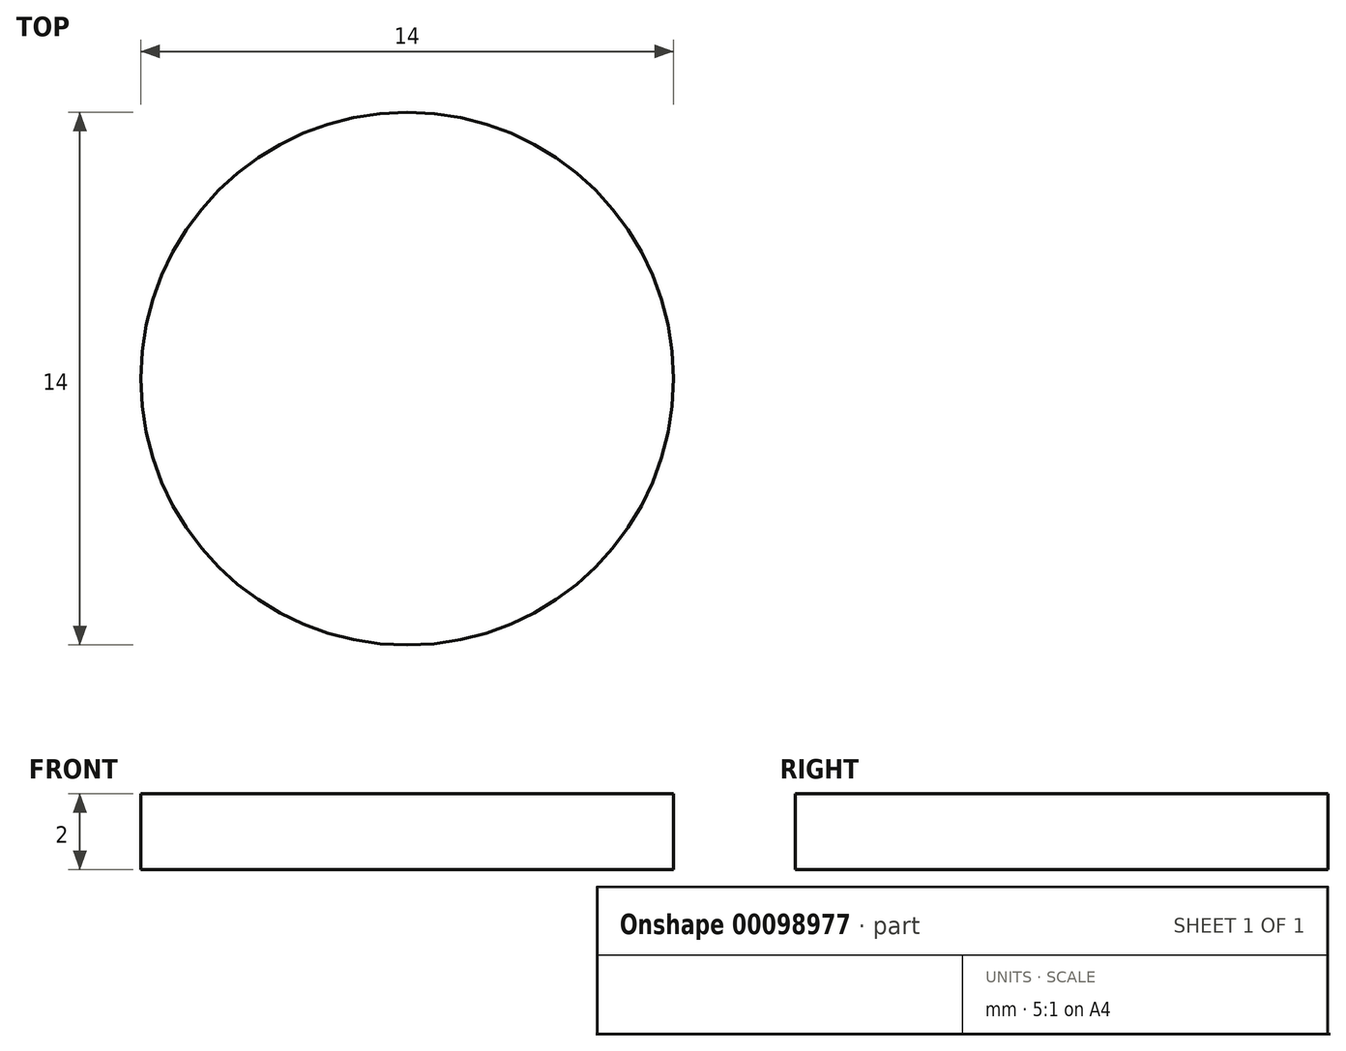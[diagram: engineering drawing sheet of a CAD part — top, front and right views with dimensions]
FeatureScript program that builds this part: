
annotation { "Feature Type Name" : "Feature", "Feature Type Description" : "" }
export const myFeature = defineFeature(function(context is Context, id is Id, definition is map)
    precondition{}
    {
        {
            var Q0;
            Q0=qCreatedBy(makeId("Top.planeOp"),FACE);
            var sketch = newSketch(context, id + "F0", { "sketchPlane" : qUnion([Q0])});
            skCircle(sketch, "E0", {"center": v(0, 0) * mm, "radius": 7 * mm});
            skSolve(sketch);
        }
        {
            var Q0;
            Q0 = qSketchRegion(id + "F0", true);
            extrude(context, id + "F1", {"entities" : qUnion([Q0]), "depth" : 2 * mm});
        }
    });
